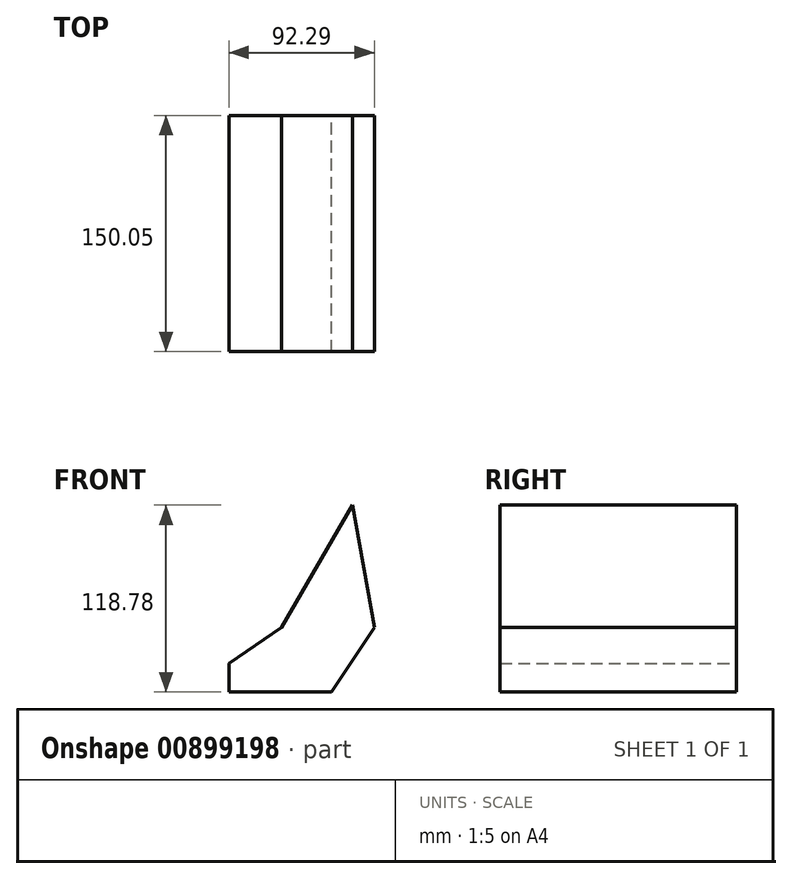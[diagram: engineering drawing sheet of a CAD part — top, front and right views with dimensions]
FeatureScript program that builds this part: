
annotation { "Feature Type Name" : "Feature", "Feature Type Description" : "" }
export const myFeature = defineFeature(function(context is Context, id is Id, definition is map)
    precondition{}
    {
        {
            var Q0;
            Q0=qCreatedBy(makeId("Front.planeOp"),FACE);
            var sketch = newSketch(context, id + "F0", { "sketchPlane" : qUnion([Q0])});
            skLineSegment(sketch, "E0", {"start": v(0, 0) * mm, "end": v(45.3, 77.55) * mm});
            skLineSegment(sketch, "E1", {"start": v(45.3, 77.55) * mm, "end": v(59, 0) * mm});
            skLineSegment(sketch, "E2", {"start": v(59, 0) * mm, "end": v(31.85, -41.23) * mm});
            skLineSegment(sketch, "E3", {"start": v(31.85, -41.23) * mm, "end": v(-33.29, -41.23) * mm});
            skLineSegment(sketch, "E4", {"start": v(-33.29, -41.23) * mm, "end": v(-33.29, -23.01) * mm});
            skLineSegment(sketch, "E5", {"start": v(-33.29, -23.01) * mm, "end": v(0, 0) * mm});
            skSolve(sketch);
        }
        {
            var Q0;
            Q0 = qSketchRegion(id + "F0", true);
            extrude(context, id + "F1", {"entities" : qUnion([Q0]), "depth" : 150.05 * mm, "offsetDistance" : 25 * mm});
        }
    });
